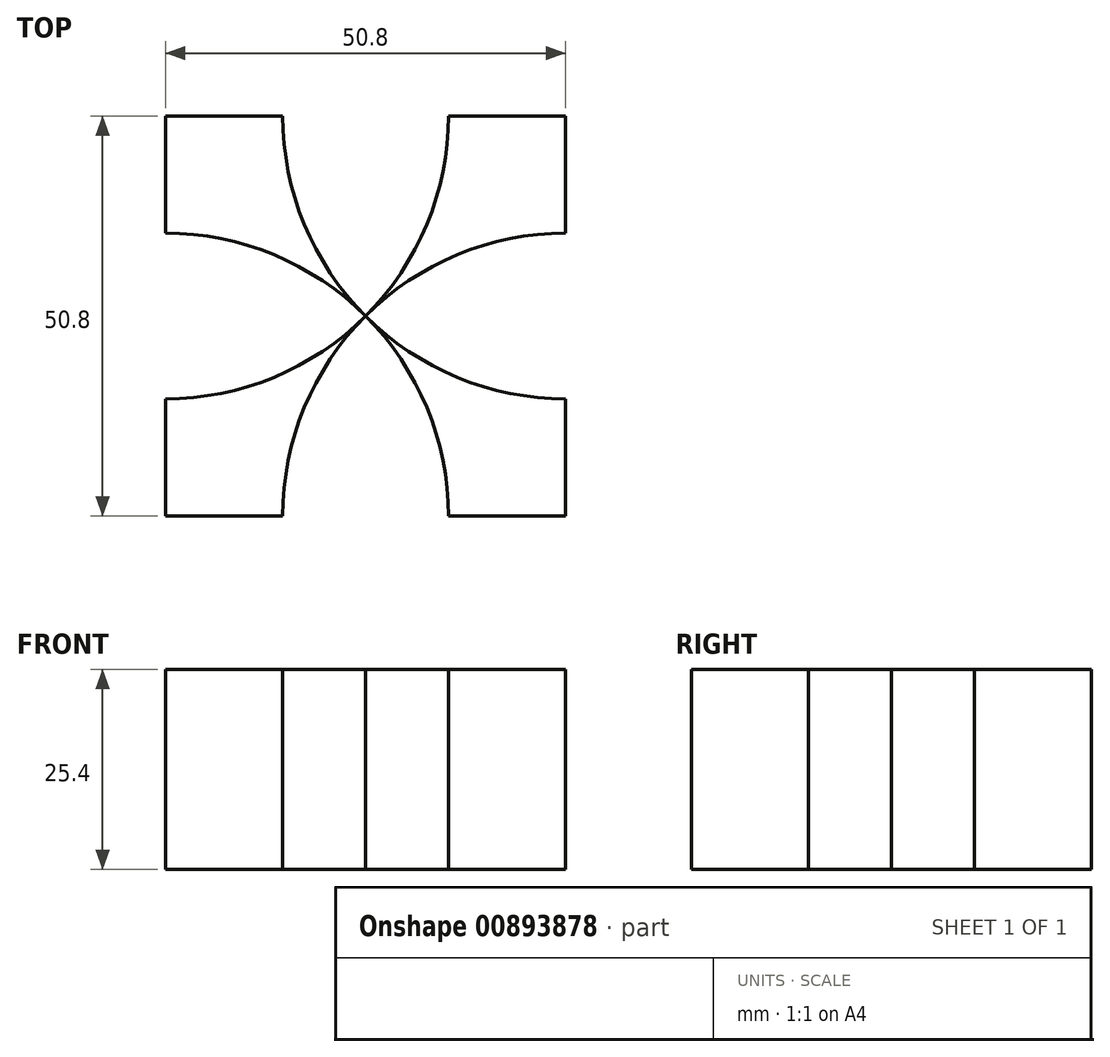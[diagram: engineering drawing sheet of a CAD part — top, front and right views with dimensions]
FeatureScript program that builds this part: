
annotation { "Feature Type Name" : "Feature", "Feature Type Description" : "" }
export const myFeature = defineFeature(function(context is Context, id is Id, definition is map)
    precondition{}
    {
        {
            var Q0;
            Q0=qCreatedBy(makeId("Top.planeOp"),FACE);
            var sketch = newSketch(context, id + "F0", { "sketchPlane" : qUnion([Q0])});
            skLineSegment(sketch, "E0.bottom", {"start": v(0, 50.8) * mm, "end": v(0, 50.8) * mm});
            skLineSegment(sketch, "E0.top", {"start": v(0, -50.8) * mm, "end": v(0, -50.8) * mm});
            skLineSegment(sketch, "E0.left", {"start": v(-50.8, 0) * mm, "end": v(-50.8, 0) * mm});
            skLineSegment(sketch, "E0.right", {"start": v(50.8, 0) * mm, "end": v(50.8, 0) * mm});
            skPoint(sketch, "E0.middle", {"position": v(0, 0) * mm});
            skPoint(sketch, "E1.visualSharp", {"position": v(-50.8, 50.8) * mm});
            skArc(sketch, "E1.filletArc", {"start": v(0, 50.8) * mm, "mid": v(-35.92, 35.92) * mm, "end": v(-50.8, 0) * mm});
            skPoint(sketch, "E2.visualSharp", {"position": v(-50.8, -50.8) * mm});
            skArc(sketch, "E2.filletArc", {"start": v(-50.8, 0) * mm, "mid": v(-35.92, -35.92) * mm, "end": v(0, -50.8) * mm});
            skPoint(sketch, "E3.visualSharp", {"position": v(50.8, -50.8) * mm});
            skArc(sketch, "E3.filletArc", {"start": v(0, -50.8) * mm, "mid": v(35.92, -35.92) * mm, "end": v(50.8, 0) * mm});
            skPoint(sketch, "E4.visualSharp", {"position": v(50.8, 50.8) * mm});
            skArc(sketch, "E4.filletArc", {"start": v(50.8, 0) * mm, "mid": v(35.92, 35.92) * mm, "end": v(0, 50.8) * mm});
            skArc(sketch, "E5", {"start": v(0, 50.8) * mm, "mid": v(0, 0) * mm, "end": v(50.8, 0) * mm});
            skArc(sketch, "E6", {"start": v(-50.8, 0) * mm, "mid": v(0, 0) * mm, "end": v(0, 50.8) * mm});
            skArc(sketch, "E7", {"start": v(0, -50.8) * mm, "mid": v(0, 0) * mm, "end": v(-50.8, 0) * mm});
            skArc(sketch, "E8", {"start": v(50.8, 0) * mm, "mid": v(0, 0) * mm, "end": v(0, -50.8) * mm});
            skLineSegment(sketch, "E9.bottom", {"start": v(-25.4, 25.4) * mm, "end": v(25.4, 25.4) * mm});
            skLineSegment(sketch, "E9.top", {"start": v(-25.4, -25.4) * mm, "end": v(25.4, -25.4) * mm});
            skLineSegment(sketch, "E9.left", {"start": v(-25.4, 25.4) * mm, "end": v(-25.4, -25.4) * mm});
            skLineSegment(sketch, "E9.right", {"start": v(25.4, 25.4) * mm, "end": v(25.4, -25.4) * mm});
            skLineSegment(sketch, "E10.0", {"start": v(-29.21, 29.21) * mm, "end": v(29.21, 29.21) * mm});
            skLineSegment(sketch, "E10.1", {"start": v(-29.21, 29.21) * mm, "end": v(-29.21, -29.21) * mm});
            skLineSegment(sketch, "E10.2", {"start": v(-29.21, -29.21) * mm, "end": v(29.21, -29.21) * mm});
            skLineSegment(sketch, "E10.3", {"start": v(29.21, 29.21) * mm, "end": v(29.21, -29.21) * mm});
            skSolve(sketch);
        }
        {
            var Q0;
            {var subQ0=sQuery(id+"F0.wireOp",EDGE,"E9.bottom");var subQ5=sQuery(id+"F0.wireOp",EDGE,"E9.left");var subQ7=makeQuery(id+"F0.imprint","INTERSECT",VERTEX,{"derivedFrom":[subQ0,subQ5]});Q0=makeQuery(id+"F0.imprint","IMPRINT",FACE,{"disambiguationData":[TD([[makeQuery(id+"F0.imprint","IMPRINT",EDGE,{"disambiguationData":[TD([[subQ7,-1.0]])],"derivedFrom":subQ0}),-1.0]])]});}
            var Q1;
            {var subQ0=sQuery(id+"F0.wireOp",EDGE,"E9.left");var subQ5=sQuery(id+"F0.wireOp",EDGE,"E9.top");var subQ7=makeQuery(id+"F0.imprint","INTERSECT",VERTEX,{"derivedFrom":[subQ5,subQ0]});Q1=makeQuery(id+"F0.imprint","IMPRINT",FACE,{"disambiguationData":[TD([[makeQuery(id+"F0.imprint","IMPRINT",EDGE,{"disambiguationData":[TD([[subQ7,-1.0]])],"derivedFrom":subQ5}),1.0]])]});}
            var Q2;
            {var subQ0=sQuery(id+"F0.wireOp",EDGE,"E9.right");var subQ5=sQuery(id+"F0.wireOp",EDGE,"E9.top");var subQ7=makeQuery(id+"F0.imprint","INTERSECT",VERTEX,{"derivedFrom":[subQ5,subQ0]});Q2=makeQuery(id+"F0.imprint","IMPRINT",FACE,{"disambiguationData":[TD([[makeQuery(id+"F0.imprint","IMPRINT",EDGE,{"disambiguationData":[TD([[subQ7,1.0]])],"derivedFrom":subQ5}),1.0]])]});}
            var Q3;
            {var subQ0=sQuery(id+"F0.wireOp",EDGE,"E9.bottom");var subQ5=sQuery(id+"F0.wireOp",EDGE,"E9.right");var subQ7=makeQuery(id+"F0.imprint","INTERSECT",VERTEX,{"derivedFrom":[subQ0,subQ5]});Q3=makeQuery(id+"F0.imprint","IMPRINT",FACE,{"disambiguationData":[TD([[makeQuery(id+"F0.imprint","IMPRINT",EDGE,{"disambiguationData":[TD([[subQ7,1.0]])],"derivedFrom":subQ0}),-1.0]])]});}
            extrude(context, id + "F1", {"entities" : qUnion([Q0, Q1, Q2, Q3]), "depth" : 25.4 * mm, "offsetDistance" : 25.4 * mm});
        }
    });
